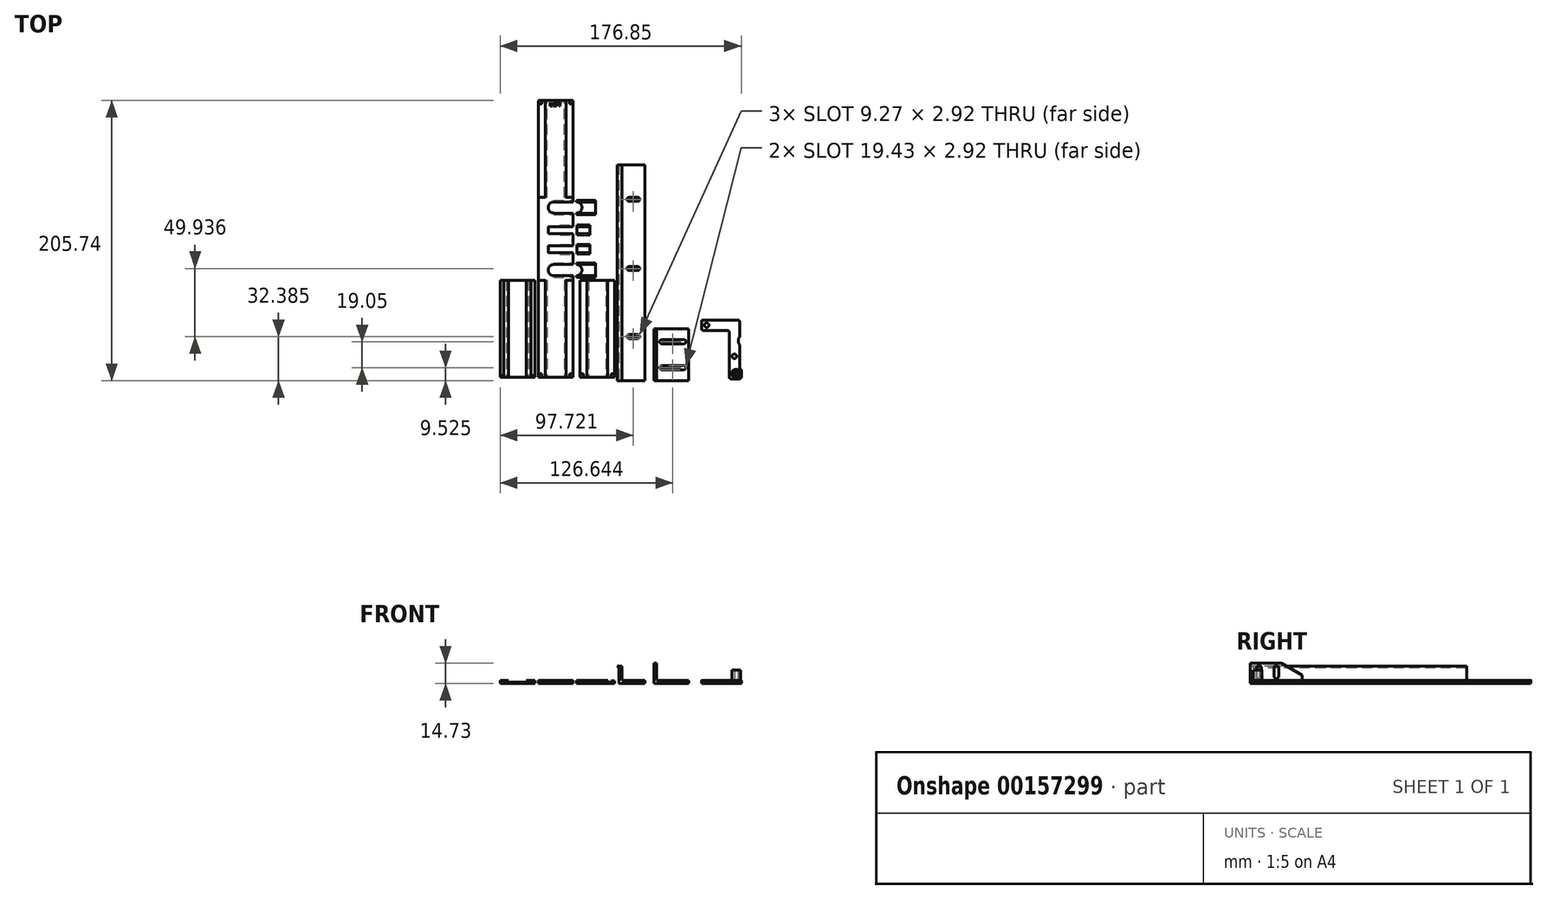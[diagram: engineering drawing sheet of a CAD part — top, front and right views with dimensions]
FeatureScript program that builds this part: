
annotation { "Feature Type Name" : "Feature", "Feature Type Description" : "" }
export const myFeature = defineFeature(function(context is Context, id is Id, definition is map)
    precondition{}
    {
        {
            var Q0;
            Q0=qCreatedBy(makeId("Top.planeOp"),FACE);
            var sketch = newSketch(context, id + "F0", { "sketchPlane" : qUnion([Q0])});
            skLineSegment(sketch, "E0.bottom", {"start": v(-2.54, 205.74) * mm, "end": v(-27.94, 205.74) * mm});
            skLineSegment(sketch, "E0.top", {"start": v(-2.54, 2.54) * mm, "end": v(-27.94, 2.54) * mm});
            skLineSegment(sketch, "E0.left", {"start": v(-2.54, 205.74) * mm, "end": v(-2.54, 131.27) * mm});
            skLineSegment(sketch, "E0.right", {"start": v(-27.94, 205.74) * mm, "end": v(-27.94, 2.54) * mm});
            skLineSegment(sketch, "E1.bottom", {"start": v(-30.48, 2.54) * mm, "end": v(-55.88, 2.54) * mm});
            skLineSegment(sketch, "E1.top", {"start": v(-30.48, 73.66) * mm, "end": v(-55.88, 73.66) * mm});
            skLineSegment(sketch, "E1.left", {"start": v(-30.48, 2.54) * mm, "end": v(-30.48, 73.66) * mm});
            skLineSegment(sketch, "E1.right", {"start": v(-55.88, 2.54) * mm, "end": v(-55.88, 73.66) * mm});
            skLineSegment(sketch, "E2.MirrorCS", {"start": v(2.54, 2.54) * mm, "end": v(2.54, 73.66) * mm});
            skLineSegment(sketch, "E3.MirrorCS", {"start": v(2.54, 73.66) * mm, "end": v(27.94, 73.66) * mm});
            skLineSegment(sketch, "E4.MirrorCS", {"start": v(27.94, 2.54) * mm, "end": v(27.94, 73.66) * mm});
            skLineSegment(sketch, "E5.MirrorCS", {"start": v(2.54, 2.54) * mm, "end": v(27.94, 2.54) * mm});
            skPoint(sketch, "E6.MirrorCS.start.orphan", {"position": v(-30.48, 73.66) * mm});
            skArc(sketch, "E7", {"start": v(-16.51, 131.27) * mm, "mid": v(-20.64, 127.14) * mm, "end": v(-16.51, 123.01) * mm});
            skArc(sketch, "E8", {"start": v(-16.51, 85.3) * mm, "mid": v(-20.64, 81.17) * mm, "end": v(-16.51, 77.04) * mm});
            skLineSegment(sketch, "E9", {"start": v(-16.51, 131.27) * mm, "end": v(-2.54, 131.27) * mm});
            skLineSegment(sketch, "E10", {"start": v(-16.51, 123.01) * mm, "end": v(-2.54, 123.01) * mm});
            skLineSegment(sketch, "E11", {"start": v(-16.51, 85.3) * mm, "end": v(-2.54, 85.3) * mm});
            skLineSegment(sketch, "E12", {"start": v(-16.51, 77.04) * mm, "end": v(-2.54, 77.04) * mm});
            skLineSegment(sketch, "E13.bottom", {"start": v(0, 77.04) * mm, "end": v(13.97, 77.04) * mm});
            skLineSegment(sketch, "E13.top", {"start": v(0, 85.3) * mm, "end": v(13.97, 85.3) * mm});
            skLineSegment(sketch, "E13.right", {"start": v(13.97, 77.04) * mm, "end": v(13.97, 85.3) * mm});
            skLineSegment(sketch, "E14.bottom", {"start": v(0, 123.01) * mm, "end": v(13.97, 123.01) * mm});
            skLineSegment(sketch, "E14.top", {"start": v(0, 131.27) * mm, "end": v(13.97, 131.27) * mm});
            skLineSegment(sketch, "E14.right", {"start": v(13.97, 123.01) * mm, "end": v(13.97, 131.27) * mm});
            skArc(sketch, "E15", {"start": v(0, 77.04) * mm, "mid": v(4.13, 81.17) * mm, "end": v(0, 85.3) * mm});
            skArc(sketch, "E16", {"start": v(0, 123.01) * mm, "mid": v(4.13, 127.14) * mm, "end": v(0, 131.27) * mm});
            skLineSegment(sketch, "E17.bottom", {"start": v(-2.54, 93.87) * mm, "end": v(-20.13, 93.87) * mm});
            skLineSegment(sketch, "E17.top", {"start": v(-2.54, 98.95) * mm, "end": v(-20.13, 98.95) * mm});
            skLineSegment(sketch, "E17.right", {"start": v(-20.64, 94.37) * mm, "end": v(-20.64, 98.44) * mm});
            skLineSegment(sketch, "E18.bottom", {"start": v(-2.54, 108.09) * mm, "end": v(-20.13, 108.09) * mm});
            skLineSegment(sketch, "E18.top", {"start": v(-2.54, 113.17) * mm, "end": v(-20.13, 113.17) * mm});
            skLineSegment(sketch, "E18.right", {"start": v(-20.64, 108.6) * mm, "end": v(-20.64, 112.66) * mm});
            skPoint(sketch, "E19.visualSharp", {"position": v(-20.64, 113.17) * mm});
            skArc(sketch, "E19.filletArc", {"start": v(-20.13, 113.17) * mm, "mid": v(-20.49, 113.02) * mm, "end": v(-20.64, 112.66) * mm});
            skPoint(sketch, "E20.visualSharp", {"position": v(-20.64, 108.09) * mm});
            skArc(sketch, "E20.filletArc", {"start": v(-20.64, 108.6) * mm, "mid": v(-20.49, 108.24) * mm, "end": v(-20.13, 108.09) * mm});
            skPoint(sketch, "E21.visualSharp", {"position": v(-20.64, 98.95) * mm});
            skArc(sketch, "E21.filletArc", {"start": v(-20.13, 98.95) * mm, "mid": v(-20.49, 98.8) * mm, "end": v(-20.64, 98.44) * mm});
            skPoint(sketch, "E22.visualSharp", {"position": v(-20.64, 93.87) * mm});
            skArc(sketch, "E22.filletArc", {"start": v(-20.64, 94.37) * mm, "mid": v(-20.49, 94.01) * mm, "end": v(-20.13, 93.87) * mm});
            skLineSegment(sketch, "E23.bottom", {"start": v(0.42, 113.17) * mm, "end": v(9.95, 113.17) * mm});
            skLineSegment(sketch, "E23.top", {"start": v(0.42, 108.09) * mm, "end": v(9.95, 108.09) * mm});
            skLineSegment(sketch, "E23.left", {"start": v(0.42, 113.17) * mm, "end": v(0.42, 108.09) * mm});
            skLineSegment(sketch, "E23.right", {"start": v(9.95, 113.17) * mm, "end": v(9.95, 108.09) * mm});
            skLineSegment(sketch, "E24.bottom", {"start": v(0.42, 98.95) * mm, "end": v(9.95, 98.95) * mm});
            skLineSegment(sketch, "E24.top", {"start": v(0.42, 93.9) * mm, "end": v(9.95, 93.9) * mm});
            skLineSegment(sketch, "E24.left", {"start": v(0.42, 98.95) * mm, "end": v(0.42, 93.9) * mm});
            skLineSegment(sketch, "E24.right", {"start": v(9.95, 98.95) * mm, "end": v(9.95, 93.9) * mm});
            skLineSegment(sketch, "E25.trimOffspring", {"start": v(-2.54, 77.04) * mm, "end": v(-2.54, 2.54) * mm});
            skLineSegment(sketch, "E26.trimOffspring", {"start": v(-2.54, 123.01) * mm, "end": v(-2.54, 113.17) * mm});
            skLineSegment(sketch, "E27.trimOffspring", {"start": v(-2.54, 108.09) * mm, "end": v(-2.54, 98.95) * mm});
            skLineSegment(sketch, "E28.trimOffspring", {"start": v(-2.54, 93.87) * mm, "end": v(-2.54, 85.3) * mm});
            skSolve(sketch);
        }
        {
            var Q0;
            Q0 = qSketchRegion(id + "F0", true);
            extrude(context, id + "F1", {"entities" : qUnion([Q0]), "depth" : 2.3 * mm});
        }
        {
            var Q0;
            Q0=makeQuery(id+"F1.opExtrude","SWEPT_FACE",FACE,{"disambiguationData":[OSD([sQuery(id+"F0.wireOp",EDGE,"E0.top")])]});
            var sketch = newSketch(context, id + "F2", { "sketchPlane" : qUnion([Q0])});
            skLineSegment(sketch, "E29", {"start": v(-22.81, 1.98) * mm, "end": v(-21.59, 0.76) * mm});
            skLineSegment(sketch, "E30", {"start": v(-21.59, 0.76) * mm, "end": v(-27.94, 0.76) * mm});
            skLineSegment(sketch, "E31", {"start": v(-27.94, 0.76) * mm, "end": v(-27.94, 2.29) * mm});
            skLineSegment(sketch, "E32", {"start": v(-8.9, 0.76) * mm, "end": v(-7.67, 1.98) * mm});
            skLineSegment(sketch, "E33", {"start": v(-2.54, 2.29) * mm, "end": v(-2.54, 0.76) * mm});
            skLineSegment(sketch, "E34", {"start": v(-2.54, 0.76) * mm, "end": v(-8.9, 0.76) * mm});
            skPoint(sketch, "E35.visualSharp", {"position": v(-23.11, 2.29) * mm});
            skArc(sketch, "E36.filletArc", {"start": v(-22.68, 2.29) * mm, "mid": v(-22.85, 2.18) * mm, "end": v(-22.81, 1.98) * mm});
            skArc(sketch, "E37.filletArc", {"start": v(-7.67, 1.98) * mm, "mid": v(-7.63, 2.18) * mm, "end": v(-7.8, 2.29) * mm});
            skLineSegment(sketch, "E38", {"start": v(-7.8, 2.29) * mm, "end": v(-2.54, 2.29) * mm});
            skLineSegment(sketch, "E39", {"start": v(-27.94, 2.29) * mm, "end": v(-22.68, 2.29) * mm});
            skLineSegment(sketch, "E40", {"start": v(-49.78, 2.29) * mm, "end": v(-51.3, 0.76) * mm});
            skLineSegment(sketch, "E41", {"start": v(-35.05, 0.76) * mm, "end": v(-36.58, 2.29) * mm});
            skLineSegment(sketch, "E42", {"start": v(-36.58, 2.29) * mm, "end": v(-49.78, 2.29) * mm});
            skLineSegment(sketch, "E43", {"start": v(-51.3, 0.76) * mm, "end": v(-35.05, 0.76) * mm});
            skLineSegment(sketch, "E44.MirrorCS", {"start": v(2.54, 2.29) * mm, "end": v(2.54, 0.76) * mm});
            skLineSegment(sketch, "E45.MirrorCS", {"start": v(2.54, 0.76) * mm, "end": v(8.9, 0.76) * mm});
            skLineSegment(sketch, "E46.MirrorCS", {"start": v(8.9, 0.76) * mm, "end": v(7.67, 1.98) * mm});
            skLineSegment(sketch, "E47.MirrorCS", {"start": v(7.8, 2.29) * mm, "end": v(2.54, 2.29) * mm});
            skArc(sketch, "E48.MirrorCS", {"start": v(7.67, 1.98) * mm, "mid": v(7.63, 2.18) * mm, "end": v(7.8, 2.29) * mm});
            skLineSegment(sketch, "E49.MirrorCS", {"start": v(27.94, 0.76) * mm, "end": v(27.94, 2.29) * mm});
            skLineSegment(sketch, "E50.MirrorCS", {"start": v(27.94, 2.29) * mm, "end": v(22.68, 2.29) * mm});
            skLineSegment(sketch, "E51.MirrorCS", {"start": v(21.59, 0.76) * mm, "end": v(27.94, 0.76) * mm});
            skLineSegment(sketch, "E52.MirrorCS", {"start": v(22.81, 1.98) * mm, "end": v(21.59, 0.76) * mm});
            skArc(sketch, "E53.MirrorCS", {"start": v(22.68, 2.29) * mm, "mid": v(22.85, 2.18) * mm, "end": v(22.81, 1.98) * mm});
            skSolve(sketch);
        }
        {
            var Q0;
            Q0 = qSketchRegion(id + "F2", true);
            extrude(context, id + "F3", {"entities" : qUnion([Q0]), "operationType" : NewBodyOperationType.REMOVE, "oppositeDirection" : true, "depth" : 71.12 * mm});
        }
        {
            var Q0;
            Q0=makeQuery(id+"F1.opExtrude","SWEPT_FACE",FACE,{"disambiguationData":[OSD([sQuery(id+"F0.wireOp",EDGE,"E0.bottom")])]});
            var sketch = newSketch(context, id + "F4", { "sketchPlane" : qUnion([Q0])});
            skLineSegment(sketch, "E54", {"start": v(7.67, 1.98) * mm, "end": v(8.9, 0.76) * mm});
            skLineSegment(sketch, "E55", {"start": v(8.9, 0.76) * mm, "end": v(2.54, 0.76) * mm});
            skLineSegment(sketch, "E56", {"start": v(2.54, 0.76) * mm, "end": v(2.54, 2.29) * mm});
            skLineSegment(sketch, "E57", {"start": v(21.59, 0.76) * mm, "end": v(22.81, 1.98) * mm});
            skLineSegment(sketch, "E58", {"start": v(27.94, 2.29) * mm, "end": v(27.94, 0.76) * mm});
            skLineSegment(sketch, "E59", {"start": v(27.94, 0.76) * mm, "end": v(21.59, 0.76) * mm});
            skPoint(sketch, "E60.visualSharp", {"position": v(7.37, 2.28) * mm});
            skArc(sketch, "E61.filletArc", {"start": v(7.8, 2.29) * mm, "mid": v(7.63, 2.18) * mm, "end": v(7.67, 1.98) * mm});
            skArc(sketch, "E62.filletArc", {"start": v(22.81, 1.98) * mm, "mid": v(22.85, 2.18) * mm, "end": v(22.68, 2.29) * mm});
            skLineSegment(sketch, "E63", {"start": v(22.68, 2.29) * mm, "end": v(27.94, 2.29) * mm});
            skLineSegment(sketch, "E64", {"start": v(2.54, 2.29) * mm, "end": v(7.8, 2.29) * mm});
            skSolve(sketch);
        }
        {
            var Q0;
            Q0 = qSketchRegion(id + "F4", true);
            extrude(context, id + "F5", {"entities" : qUnion([Q0]), "operationType" : NewBodyOperationType.REMOVE, "oppositeDirection" : true, "depth" : 71.12 * mm});
        }
        {
            var Q0;
            Q0=makeQuery(id+"F3.boolean.opBoolean","COPY",FACE,{"derivedFrom":makeQuery(id+"F3.opExtrude","SWEPT_FACE",FACE,{"disambiguationData":[OSD([sQuery(id+"F2.wireOp",EDGE,"E34")])]})});
            var sketch = newSketch(context, id + "F6", { "sketchPlane" : qUnion([Q0])});
            skLineSegment(sketch, "E65.bottom", {"start": v(-2.54, 2.54) * mm, "end": v(-5.08, 2.54) * mm});
            skLineSegment(sketch, "E65.top", {"start": v(-2.54, 5.08) * mm, "end": v(-5.08, 5.08) * mm});
            skLineSegment(sketch, "E65.left", {"start": v(-2.54, 2.54) * mm, "end": v(-2.54, 5.08) * mm});
            skLineSegment(sketch, "E65.right", {"start": v(-5.08, 2.54) * mm, "end": v(-5.08, 5.08) * mm});
            skLineSegment(sketch, "E66.bottom", {"start": v(-25.4, 2.54) * mm, "end": v(-27.94, 2.54) * mm});
            skLineSegment(sketch, "E66.top", {"start": v(-25.4, 5.08) * mm, "end": v(-27.94, 5.08) * mm});
            skLineSegment(sketch, "E66.left", {"start": v(-25.4, 2.54) * mm, "end": v(-25.4, 5.08) * mm});
            skLineSegment(sketch, "E66.right", {"start": v(-27.94, 2.54) * mm, "end": v(-27.94, 5.08) * mm});
            skLineSegment(sketch, "E67.bottom", {"start": v(27.94, 2.54) * mm, "end": v(25.4, 2.54) * mm});
            skLineSegment(sketch, "E67.top", {"start": v(27.94, 5.08) * mm, "end": v(25.4, 5.08) * mm});
            skLineSegment(sketch, "E67.left", {"start": v(27.94, 2.54) * mm, "end": v(27.94, 5.08) * mm});
            skLineSegment(sketch, "E67.right", {"start": v(25.4, 2.54) * mm, "end": v(25.4, 5.08) * mm});
            skLineSegment(sketch, "E68.bottom", {"start": v(5.08, 2.54) * mm, "end": v(2.54, 2.54) * mm});
            skLineSegment(sketch, "E68.top", {"start": v(5.08, 5.08) * mm, "end": v(2.54, 5.08) * mm});
            skLineSegment(sketch, "E68.left", {"start": v(5.08, 2.54) * mm, "end": v(5.08, 5.08) * mm});
            skLineSegment(sketch, "E68.right", {"start": v(2.54, 2.54) * mm, "end": v(2.54, 5.08) * mm});
            skLineSegment(sketch, "E69.bottom", {"start": v(-27.94, 205.74) * mm, "end": v(-25.4, 205.74) * mm});
            skLineSegment(sketch, "E69.top", {"start": v(-27.94, 203.2) * mm, "end": v(-25.4, 203.2) * mm});
            skLineSegment(sketch, "E69.left", {"start": v(-27.94, 205.74) * mm, "end": v(-27.94, 203.2) * mm});
            skLineSegment(sketch, "E69.right", {"start": v(-25.4, 205.74) * mm, "end": v(-25.4, 203.2) * mm});
            skLineSegment(sketch, "E70.bottom", {"start": v(-5.08, 205.74) * mm, "end": v(-2.54, 205.74) * mm});
            skLineSegment(sketch, "E70.top", {"start": v(-5.08, 203.2) * mm, "end": v(-2.54, 203.2) * mm});
            skLineSegment(sketch, "E70.left", {"start": v(-5.08, 205.74) * mm, "end": v(-5.08, 203.2) * mm});
            skLineSegment(sketch, "E70.right", {"start": v(-2.54, 205.74) * mm, "end": v(-2.54, 203.2) * mm});
            skSolve(sketch);
        }
        {
            var Q0;
            Q0 = qSketchRegion(id + "F6", true);
            extrude(context, id + "F7", {"entities" : qUnion([Q0]), "operationType" : NewBodyOperationType.ADD, "depth" : 1.14 * mm});
        }
        {
            var Q0;
            {var subQ0=sQuery(id+"F0.wireOp",EDGE,"E1.bottom");var subQ1=sQuery(id+"F0.wireOp",EDGE,"E1.top");var subQ2=sQuery(id+"F0.wireOp",EDGE,"E1.right");Q0=makeQuery(id+"F3.boolean.opBoolean","SPLIT",FACE,{"disambiguationData":[TD([makeQuery(id+"F1.opExtrude","SWEPT_FACE",FACE,{"disambiguationData":[OSD([subQ2])]})])],"derivedFrom":makeQuery(id+"F1.opExtrude","CAP_FACE",FACE,{"disambiguationData":[OSD([subQ0,subQ1,sQuery(id+"F0.wireOp",EDGE,"E1.left"),subQ2])],"isStart":false})});}
            var sketch = newSketch(context, id + "F8", { "sketchPlane" : qUnion([Q0])});
            skLineSegment(sketch, "E71.bottom", {"start": v(-30.48, 3.8) * mm, "end": v(-33.27, 3.8) * mm});
            skLineSegment(sketch, "E71.top", {"start": v(-30.48, 73.66) * mm, "end": v(-33.27, 73.66) * mm});
            skLineSegment(sketch, "E71.left", {"start": v(-30.48, 3.8) * mm, "end": v(-30.48, 73.66) * mm});
            skLineSegment(sketch, "E71.right", {"start": v(-33.27, 3.8) * mm, "end": v(-33.27, 73.66) * mm});
            skLineSegment(sketch, "E72.bottom", {"start": v(-53.09, 3.8) * mm, "end": v(-55.88, 3.8) * mm});
            skLineSegment(sketch, "E72.top", {"start": v(-53.09, 73.66) * mm, "end": v(-55.88, 73.66) * mm});
            skLineSegment(sketch, "E72.left", {"start": v(-53.09, 3.8) * mm, "end": v(-53.09, 73.66) * mm});
            skLineSegment(sketch, "E72.right", {"start": v(-55.88, 3.8) * mm, "end": v(-55.88, 73.66) * mm});
            skSolve(sketch);
        }
        {
            var Q0;
            Q0 = qSketchRegion(id + "F8", true);
            extrude(context, id + "F9", {"entities" : qUnion([Q0]), "operationType" : NewBodyOperationType.REMOVE, "oppositeDirection" : true, "depth" : 1.27 * mm});
        }
        {
            var Q0;
            Q0=makeQuery(id+"F1.opExtrude","SWEPT_FACE",FACE,{"disambiguationData":[OSD([sQuery(id+"F0.wireOp",EDGE,"E28.trimOffspring")])]});
            var sketch = newSketch(context, id + "F10", { "sketchPlane" : qUnion([Q0])});
            skLineSegment(sketch, "E73", {"start": v(85.3, 2.29) * mm, "end": v(86.44, 1.14) * mm});
            skLineSegment(sketch, "E74", {"start": v(86.44, 1.14) * mm, "end": v(85.3, 0) * mm});
            skLineSegment(sketch, "E75", {"start": v(123.01, 2.29) * mm, "end": v(121.87, 1.14) * mm});
            skLineSegment(sketch, "E76", {"start": v(121.87, 1.14) * mm, "end": v(123.01, 0) * mm});
            skLineSegment(sketch, "E77", {"start": v(123.01, 0) * mm, "end": v(123.01, 2.29) * mm});
            skLineSegment(sketch, "E78", {"start": v(131.27, 2.29) * mm, "end": v(132.41, 1.14) * mm});
            skLineSegment(sketch, "E79", {"start": v(132.41, 1.14) * mm, "end": v(131.27, 0) * mm});
            skLineSegment(sketch, "E80", {"start": v(131.27, 0) * mm, "end": v(131.27, 2.29) * mm});
            skLineSegment(sketch, "E81", {"start": v(85.3, 2.29) * mm, "end": v(85.3, 0) * mm});
            skLineSegment(sketch, "E82", {"start": v(77.04, 2.29) * mm, "end": v(75.9, 1.14) * mm});
            skLineSegment(sketch, "E83", {"start": v(75.9, 1.14) * mm, "end": v(77.04, 0) * mm});
            skLineSegment(sketch, "E84", {"start": v(77.04, 0) * mm, "end": v(77.04, 2.29) * mm});
            skSolve(sketch);
        }
        {
            var Q0;
            Q0 = qSketchRegion(id + "F10", true);
            extrude(context, id + "F11", {"entities" : qUnion([Q0]), "operationType" : NewBodyOperationType.REMOVE, "oppositeDirection" : true, "depth" : 13.97 * mm});
        }
        {
            var Q0;
            Q0=makeQuery(id+"F1.opExtrude","SWEPT_FACE",FACE,{"disambiguationData":[OSD([sQuery(id+"F0.wireOp",EDGE,"E13.right")])]});
            var sketch = newSketch(context, id + "F12", { "sketchPlane" : qUnion([Q0])});
            skLineSegment(sketch, "E85", {"start": v(77.04, 2.16) * mm, "end": v(76.02, 1.14) * mm});
            skLineSegment(sketch, "E86", {"start": v(76.02, 1.14) * mm, "end": v(77.04, 0.13) * mm});
            skLineSegment(sketch, "E87", {"start": v(77.04, 0.13) * mm, "end": v(77.04, 2.16) * mm});
            skLineSegment(sketch, "E88", {"start": v(85.3, 0.13) * mm, "end": v(86.3, 1.14) * mm});
            skLineSegment(sketch, "E89", {"start": v(86.3, 1.14) * mm, "end": v(85.3, 2.16) * mm});
            skLineSegment(sketch, "E90", {"start": v(85.3, 2.16) * mm, "end": v(85.3, 0.13) * mm});
            skLineSegment(sketch, "E91", {"start": v(123.01, 2.16) * mm, "end": v(122, 1.14) * mm});
            skLineSegment(sketch, "E92", {"start": v(122, 1.14) * mm, "end": v(123.01, 0.13) * mm});
            skLineSegment(sketch, "E93", {"start": v(123.01, 0.13) * mm, "end": v(123.01, 2.16) * mm});
            skLineSegment(sketch, "E94", {"start": v(131.27, 0.13) * mm, "end": v(132.28, 1.14) * mm});
            skLineSegment(sketch, "E95", {"start": v(132.28, 1.14) * mm, "end": v(131.27, 2.16) * mm});
            skLineSegment(sketch, "E96", {"start": v(131.27, 2.16) * mm, "end": v(131.27, 0.13) * mm});
            skSolve(sketch);
        }
        {
            var Q0;
            Q0 = qSketchRegion(id + "F12", true);
            extrude(context, id + "F13", {"entities" : qUnion([Q0]), "operationType" : NewBodyOperationType.ADD, "oppositeDirection" : true, "depth" : 13.97 * mm});
        }
        {
            var Q0;
            Q0=makeQuery(id+"F1.opExtrude","SWEPT_FACE",FACE,{"disambiguationData":[OSD([sQuery(id+"F0.wireOp",EDGE,"E24.right")])]});
            var sketch = newSketch(context, id + "F14", { "sketchPlane" : qUnion([Q0])});
            skLineSegment(sketch, "E97", {"start": v(93.9, 2.16) * mm, "end": v(92.9, 1.14) * mm});
            skLineSegment(sketch, "E98", {"start": v(92.9, 1.14) * mm, "end": v(93.9, 0.13) * mm});
            skLineSegment(sketch, "E99", {"start": v(93.9, 0.13) * mm, "end": v(93.9, 2.16) * mm});
            skLineSegment(sketch, "E100", {"start": v(98.95, 2.16) * mm, "end": v(99.96, 1.14) * mm});
            skLineSegment(sketch, "E101", {"start": v(99.96, 1.14) * mm, "end": v(98.95, 0.13) * mm});
            skLineSegment(sketch, "E102", {"start": v(98.95, 0.13) * mm, "end": v(98.95, 2.16) * mm});
            skLineSegment(sketch, "E103", {"start": v(108.09, 2.16) * mm, "end": v(107.07, 1.14) * mm});
            skLineSegment(sketch, "E104", {"start": v(107.07, 1.14) * mm, "end": v(108.09, 0.13) * mm});
            skLineSegment(sketch, "E105", {"start": v(108.09, 0.13) * mm, "end": v(108.09, 2.16) * mm});
            skLineSegment(sketch, "E106", {"start": v(113.17, 2.16) * mm, "end": v(114.19, 1.14) * mm});
            skLineSegment(sketch, "E107", {"start": v(114.19, 1.14) * mm, "end": v(113.17, 0.13) * mm});
            skLineSegment(sketch, "E108", {"start": v(113.17, 0.13) * mm, "end": v(113.17, 2.16) * mm});
            skSolve(sketch);
        }
        {
            var Q0;
            Q0=makeQuery(id+"F1.opExtrude","SWEPT_FACE",FACE,{"disambiguationData":[OSD([sQuery(id+"F0.wireOp",EDGE,"E27.trimOffspring")])]});
            var sketch = newSketch(context, id + "F15", { "sketchPlane" : qUnion([Q0])});
            skLineSegment(sketch, "E109", {"start": v(93.87, 2.29) * mm, "end": v(92.72, 1.14) * mm});
            skLineSegment(sketch, "E110", {"start": v(92.72, 1.14) * mm, "end": v(93.87, 0) * mm});
            skLineSegment(sketch, "E111", {"start": v(93.87, 0) * mm, "end": v(93.87, 2.29) * mm});
            skLineSegment(sketch, "E112", {"start": v(98.95, 2.29) * mm, "end": v(100.09, 1.14) * mm});
            skLineSegment(sketch, "E113", {"start": v(100.09, 1.14) * mm, "end": v(98.95, 0) * mm});
            skLineSegment(sketch, "E114", {"start": v(98.95, 0) * mm, "end": v(98.95, 2.29) * mm});
            skLineSegment(sketch, "E115", {"start": v(113.17, 2.29) * mm, "end": v(114.31, 1.14) * mm});
            skLineSegment(sketch, "E116", {"start": v(114.31, 1.14) * mm, "end": v(113.17, 0) * mm});
            skLineSegment(sketch, "E117", {"start": v(113.17, 0) * mm, "end": v(113.17, 2.29) * mm});
            skLineSegment(sketch, "E118", {"start": v(108.09, 2.29) * mm, "end": v(106.95, 1.14) * mm});
            skLineSegment(sketch, "E119", {"start": v(106.95, 1.14) * mm, "end": v(108.09, 0) * mm});
            skLineSegment(sketch, "E120", {"start": v(108.09, 0) * mm, "end": v(108.09, 2.29) * mm});
            skSolve(sketch);
        }
        {
            var Q0;
            Q0 = qSketchRegion(id + "F15", true);
            extrude(context, id + "F16", {"entities" : qUnion([Q0]), "operationType" : NewBodyOperationType.REMOVE, "oppositeDirection" : true, "depth" : 9.52 * mm});
        }
        {
            var Q0;
            Q0 = qSketchRegion(id + "F14", true);
            extrude(context, id + "F17", {"entities" : qUnion([Q0]), "operationType" : NewBodyOperationType.ADD, "oppositeDirection" : true, "depth" : 9.52 * mm});
        }
        {
            var Q0;
            Q0=makeQuery(id+"F1.opExtrude","CAP_FACE",FACE,{"disambiguationData":[OSD([sQuery(id+"F0.wireOp",EDGE,"E0.bottom"),sQuery(id+"F0.wireOp",EDGE,"E0.top"),sQuery(id+"F0.wireOp",EDGE,"E0.left"),sQuery(id+"F0.wireOp",EDGE,"E0.right"),sQuery(id+"F0.wireOp",EDGE,"E7"),sQuery(id+"F0.wireOp",EDGE,"E8"),sQuery(id+"F0.wireOp",EDGE,"E9"),sQuery(id+"F0.wireOp",EDGE,"E10"),sQuery(id+"F0.wireOp",EDGE,"E11"),sQuery(id+"F0.wireOp",EDGE,"E12"),sQuery(id+"F0.wireOp",EDGE,"E17.bottom"),sQuery(id+"F0.wireOp",EDGE,"E17.top"),sQuery(id+"F0.wireOp",EDGE,"E17.right"),sQuery(id+"F0.wireOp",EDGE,"E18.bottom"),sQuery(id+"F0.wireOp",EDGE,"E18.top"),sQuery(id+"F0.wireOp",EDGE,"E18.right"),sQuery(id+"F0.wireOp",EDGE,"E19.filletArc"),sQuery(id+"F0.wireOp",EDGE,"E20.filletArc"),sQuery(id+"F0.wireOp",EDGE,"E21.filletArc"),sQuery(id+"F0.wireOp",EDGE,"E22.filletArc"),sQuery(id+"F0.wireOp",EDGE,"E25.trimOffspring"),sQuery(id+"F0.wireOp",EDGE,"E26.trimOffspring"),sQuery(id+"F0.wireOp",EDGE,"E27.trimOffspring"),sQuery(id+"F0.wireOp",EDGE,"E28.trimOffspring")])],"isStart":false});
            var sketch = newSketch(context, id + "F18", { "sketchPlane" : qUnion([Q0])});
            skText(sketch, "E121", { "text": "LEFT", "fontName": "OpenSans-Bold.ttf"});
            const initialGuessF18  = {"E121": [-0.01955, 0.20151, 1, 0, 0.0027]};
            skSetInitialGuess(sketch, initialGuessF18);
            skSolve(sketch);
        }
        {
            var Q0;
            Q0 = qSketchRegion(id + "F18", true);
            extrude(context, id + "F19", {"entities" : qUnion([Q0]), "operationType" : NewBodyOperationType.REMOVE, "oppositeDirection" : true, "depth" : 0.38 * mm});
        }
        {
            var Q0;
            Q0=qCreatedBy(makeId("Front.planeOp"),FACE);
            var sketch = newSketch(context, id + "F20", { "sketchPlane" : qUnion([Q0])});
            skLineSegment(sketch, "E122", {"start": v(31.3, 12.7) * mm, "end": v(31.3, 0) * mm});
            skLineSegment(sketch, "E123", {"start": v(31.3, 0) * mm, "end": v(50.35, 0) * mm});
            skLineSegment(sketch, "E124", {"start": v(50.35, 0) * mm, "end": v(50.35, 2.03) * mm});
            skLineSegment(sketch, "E125", {"start": v(50.35, 2.03) * mm, "end": v(33.33, 2.03) * mm});
            skLineSegment(sketch, "E126", {"start": v(33.33, 2.03) * mm, "end": v(33.33, 12.7) * mm});
            skLineSegment(sketch, "E127", {"start": v(31.3, 12.7) * mm, "end": v(33.33, 12.7) * mm});
            skSolve(sketch);
        }
        {
            var Q0;
            Q0 = qSketchRegion(id + "F20", true);
            extrude(context, id + "F21", {"entities" : qUnion([Q0]), "oppositeDirection" : true, "depth" : 158.52 * mm});
        }
        {
            var Q0;
            Q0=makeQuery(id+"F21.opExtrude","CAP_FACE",FACE,{"disambiguationData":[OSD([sQuery(id+"F20.wireOp",EDGE,"E122"),sQuery(id+"F20.wireOp",EDGE,"E123"),sQuery(id+"F20.wireOp",EDGE,"E124"),sQuery(id+"F20.wireOp",EDGE,"E125"),sQuery(id+"F20.wireOp",EDGE,"E126"),sQuery(id+"F20.wireOp",EDGE,"E127")])],"isStart":true});
            var sketch = newSketch(context, id + "F22", { "sketchPlane" : qUnion([Q0])});
            skLineSegment(sketch, "E128", {"start": v(31.3, 12.7) * mm, "end": v(30.03, 12.7) * mm});
            skLineSegment(sketch, "E129", {"start": v(30.03, 12.7) * mm, "end": v(31.3, 11.43) * mm});
            skLineSegment(sketch, "E130", {"start": v(31.3, 11.43) * mm, "end": v(31.3, 12.7) * mm});
            skSolve(sketch);
        }
        {
            var Q0;
            Q0 = qSketchRegion(id + "F22", true);
            extrude(context, id + "F23", {"entities" : qUnion([Q0]), "operationType" : NewBodyOperationType.ADD, "oppositeDirection" : true, "depth" : 158.52 * mm});
        }
        {
            var Q0;
            Q0=makeQuery(id+"F21.opExtrude","SWEPT_FACE",FACE,{"disambiguationData":[OSD([sQuery(id+"F20.wireOp",EDGE,"E125")])]});
            var sketch = newSketch(context, id + "F24", { "sketchPlane" : qUnion([Q0])});
            skArc(sketch, "E131", {"start": v(45.02, 30.92) * mm, "mid": v(46.48, 32.39) * mm, "end": v(45.02, 33.85) * mm});
            skArc(sketch, "E132", {"start": v(45.02, 131.66) * mm, "mid": v(46.48, 133.12) * mm, "end": v(45.02, 134.58) * mm});
            skArc(sketch, "E133", {"start": v(45.02, 80.86) * mm, "mid": v(46.48, 82.32) * mm, "end": v(45.02, 83.78) * mm});
            skArc(sketch, "E134", {"start": v(38.67, 134.58) * mm, "mid": v(37.2, 133.12) * mm, "end": v(38.67, 131.66) * mm});
            skArc(sketch, "E135", {"start": v(38.67, 83.78) * mm, "mid": v(37.2, 82.32) * mm, "end": v(38.67, 80.86) * mm});
            skArc(sketch, "E136", {"start": v(38.67, 33.85) * mm, "mid": v(37.2, 32.39) * mm, "end": v(38.67, 30.92) * mm});
            skLineSegment(sketch, "E137", {"start": v(45.02, 134.58) * mm, "end": v(38.67, 134.58) * mm});
            skLineSegment(sketch, "E138", {"start": v(38.67, 131.66) * mm, "end": v(45.02, 131.66) * mm});
            skLineSegment(sketch, "E139", {"start": v(38.67, 83.78) * mm, "end": v(45.02, 83.78) * mm});
            skLineSegment(sketch, "E140", {"start": v(38.67, 80.86) * mm, "end": v(45.02, 80.86) * mm});
            skLineSegment(sketch, "E141", {"start": v(38.67, 33.85) * mm, "end": v(45.02, 33.85) * mm});
            skLineSegment(sketch, "E142", {"start": v(45.02, 30.92) * mm, "end": v(38.67, 30.92) * mm});
            skSolve(sketch);
        }
        {
            var Q0;
            Q0 = qSketchRegion(id + "F24", true);
            extrude(context, id + "F25", {"entities" : qUnion([Q0]), "operationType" : NewBodyOperationType.REMOVE, "endBound" : BoundingType.UP_TO_NEXT, "oppositeDirection" : true, "depth" : 25.4 * mm});
        }
        {
            var Q0;
            Q0=qCreatedBy(makeId("Top.planeOp"),FACE);
            var sketch = newSketch(context, id + "F26", { "sketchPlane" : qUnion([Q0])});
            skLineSegment(sketch, "E143.bottom", {"start": v(56.92, 38.1) * mm, "end": v(82.32, 38.1) * mm});
            skLineSegment(sketch, "E143.top", {"start": v(56.92, 0) * mm, "end": v(82.32, 0) * mm});
            skLineSegment(sketch, "E143.left", {"start": v(56.92, 38.1) * mm, "end": v(56.92, 0) * mm});
            skLineSegment(sketch, "E143.right", {"start": v(82.32, 38.1) * mm, "end": v(82.32, 0) * mm});
            skArc(sketch, "E144", {"start": v(62.5, 30.04) * mm, "mid": v(61.05, 28.58) * mm, "end": v(62.5, 27.11) * mm});
            skArc(sketch, "E145", {"start": v(79.02, 27.11) * mm, "mid": v(80.48, 28.58) * mm, "end": v(79.02, 30.04) * mm});
            skArc(sketch, "E146", {"start": v(62.5, 10.99) * mm, "mid": v(61.05, 9.53) * mm, "end": v(62.5, 8.06) * mm});
            skArc(sketch, "E147", {"start": v(79.02, 8.06) * mm, "mid": v(80.48, 9.53) * mm, "end": v(79.02, 10.99) * mm});
            skLineSegment(sketch, "E148", {"start": v(62.5, 30.04) * mm, "end": v(79.02, 30.04) * mm});
            skLineSegment(sketch, "E149", {"start": v(79.02, 10.99) * mm, "end": v(62.5, 10.99) * mm});
            skLineSegment(sketch, "E150", {"start": v(62.5, 8.06) * mm, "end": v(79.02, 8.06) * mm});
            skLineSegment(sketch, "E151", {"start": v(62.5, 27.11) * mm, "end": v(79.02, 27.11) * mm});
            skSolve(sketch);
        }
        {
            var Q0;
            Q0 = qSketchRegion(id + "F26", true);
            extrude(context, id + "F27", {"entities" : qUnion([Q0]), "depth" : 2.03 * mm});
        }
        {
            var Q0;
            Q0=makeQuery(id+"F27.opExtrude","CAP_FACE",FACE,{"disambiguationData":[OSD([sQuery(id+"F26.wireOp",EDGE,"E143.bottom"),sQuery(id+"F26.wireOp",EDGE,"E143.top"),sQuery(id+"F26.wireOp",EDGE,"E143.left"),sQuery(id+"F26.wireOp",EDGE,"E143.right"),sQuery(id+"F26.wireOp",EDGE,"E144"),sQuery(id+"F26.wireOp",EDGE,"E145"),sQuery(id+"F26.wireOp",EDGE,"E146"),sQuery(id+"F26.wireOp",EDGE,"E147"),sQuery(id+"F26.wireOp",EDGE,"E148"),sQuery(id+"F26.wireOp",EDGE,"E149"),sQuery(id+"F26.wireOp",EDGE,"E150"),sQuery(id+"F26.wireOp",EDGE,"E151")])],"isStart":false});
            var sketch = newSketch(context, id + "F28", { "sketchPlane" : qUnion([Q0])});
            skLineSegment(sketch, "E152.bottom", {"start": v(56.92, 38.1) * mm, "end": v(58.95, 38.1) * mm});
            skLineSegment(sketch, "E152.top", {"start": v(56.92, 0) * mm, "end": v(58.95, 0) * mm});
            skLineSegment(sketch, "E152.left", {"start": v(56.92, 38.1) * mm, "end": v(56.92, 0) * mm});
            skLineSegment(sketch, "E152.right", {"start": v(58.95, 38.1) * mm, "end": v(58.95, 0) * mm});
            skSolve(sketch);
        }
        {
            var Q0;
            Q0 = qSketchRegion(id + "F28", true);
            extrude(context, id + "F29", {"entities" : qUnion([Q0]), "operationType" : NewBodyOperationType.ADD, "depth" : 12.7 * mm});
        }
        {
            var Q0;
            Q0=makeQuery(id+"F29.opExtrude","SWEPT_FACE",FACE,{"disambiguationData":[OSD([sQuery(id+"F28.wireOp",EDGE,"E152.right")])]});
            var sketch = newSketch(context, id + "F30", { "sketchPlane" : qUnion([Q0])});
            skArc(sketch, "E153", {"start": v(8, 11.56) * mm, "mid": v(6.35, 13.2) * mm, "end": v(4.7, 11.56) * mm});
            skArc(sketch, "E154", {"start": v(20.7, 11.56) * mm, "mid": v(19.05, 13.2) * mm, "end": v(17.4, 11.56) * mm});
            skArc(sketch, "E155", {"start": v(4.7, 5.2) * mm, "mid": v(6.35, 3.56) * mm, "end": v(8, 5.2) * mm});
            skArc(sketch, "E156", {"start": v(17.4, 5.2) * mm, "mid": v(19.05, 3.56) * mm, "end": v(20.7, 5.2) * mm});
            skLineSegment(sketch, "E157", {"start": v(4.7, 11.56) * mm, "end": v(4.7, 5.2) * mm});
            skLineSegment(sketch, "E158", {"start": v(8, 5.2) * mm, "end": v(8, 11.56) * mm});
            skLineSegment(sketch, "E159", {"start": v(17.4, 5.2) * mm, "end": v(17.4, 11.56) * mm});
            skLineSegment(sketch, "E160", {"start": v(20.7, 11.56) * mm, "end": v(20.7, 5.2) * mm});
            skLineSegment(sketch, "E161", {"start": v(22.86, 14.73) * mm, "end": v(38.1, 5.84) * mm});
            skLineSegment(sketch, "E162", {"start": v(38.1, 5.84) * mm, "end": v(38.1, 14.73) * mm});
            skLineSegment(sketch, "E163", {"start": v(38.1, 14.73) * mm, "end": v(22.86, 14.73) * mm});
            skSolve(sketch);
        }
        {
            var Q0;
            Q0 = qSketchRegion(id + "F30", true);
            extrude(context, id + "F31", {"entities" : qUnion([Q0]), "operationType" : NewBodyOperationType.REMOVE, "endBound" : BoundingType.UP_TO_NEXT, "oppositeDirection" : true, "depth" : 25.4 * mm});
        }
        {
            var Q0;
            Q0=qCreatedBy(makeId("Top.planeOp"),FACE);
            var sketch = newSketch(context, id + "F32", { "sketchPlane" : qUnion([Q0])});
            skLineSegment(sketch, "E164", {"start": v(112.08, 2.64) * mm, "end": v(112.08, 35.66) * mm});
            skLineSegment(sketch, "E165", {"start": v(91.76, 38.2) * mm, "end": v(91.76, 43.28) * mm});
            skLineSegment(sketch, "E166", {"start": v(93.03, 44.55) * mm, "end": v(118.43, 44.55) * mm});
            skLineSegment(sketch, "E167", {"start": v(119.7, 43.28) * mm, "end": v(119.7, 32.17) * mm});
            skLineSegment(sketch, "E168", {"start": v(119.7, 1.37) * mm, "end": v(113.35, 1.37) * mm});
            skCircle(sketch, "E169", {"center": v(95.57, 40.74) * mm, "radius": 1.65 * mm});
            skCircle(sketch, "E170", {"center": v(115.89, 17.88) * mm, "radius": 1.65 * mm});
            skLineSegment(sketch, "E171", {"start": v(93.03, 36.93) * mm, "end": v(110.8, 36.93) * mm});
            skPoint(sketch, "E172.visualSharp", {"position": v(119.7, 44.55) * mm});
            skArc(sketch, "E172.filletArc", {"start": v(119.7, 43.28) * mm, "mid": v(119.33, 44.18) * mm, "end": v(118.43, 44.55) * mm});
            skPoint(sketch, "E173.visualSharp", {"position": v(112.08, 36.93) * mm});
            skArc(sketch, "E173.filletArc", {"start": v(112.08, 35.66) * mm, "mid": v(111.7, 36.56) * mm, "end": v(110.8, 36.93) * mm});
            skPoint(sketch, "E174.visualSharp", {"position": v(91.76, 44.55) * mm});
            skArc(sketch, "E174.filletArc", {"start": v(93.03, 44.55) * mm, "mid": v(92.13, 44.18) * mm, "end": v(91.76, 43.28) * mm});
            skPoint(sketch, "E175.visualSharp", {"position": v(91.76, 36.93) * mm});
            skArc(sketch, "E175.filletArc", {"start": v(91.76, 38.2) * mm, "mid": v(92.13, 37.3) * mm, "end": v(93.03, 36.93) * mm});
            skLineSegment(sketch, "E176", {"start": v(120.32, 8.62) * mm, "end": v(120.35, 8.6) * mm});
            skLineSegment(sketch, "E177", {"start": v(120.97, 7.51) * mm, "end": v(120.97, 2.64) * mm});
            skLineSegment(sketch, "E178", {"start": v(119.7, 1.37) * mm, "end": v(119.7, 1.37) * mm});
            skArc(sketch, "E179", {"start": v(119.7, 32.17) * mm, "mid": v(118.75, 29.31) * mm, "end": v(119.7, 26.46) * mm});
            skLineSegment(sketch, "E180.trimOffspring", {"start": v(119.7, 26.46) * mm, "end": v(119.7, 9.71) * mm});
            skPoint(sketch, "E181.visualSharp", {"position": v(120.97, 8.24) * mm});
            skArc(sketch, "E181.filletArc", {"start": v(120.97, 7.51) * mm, "mid": v(120.8, 8.14) * mm, "end": v(120.35, 8.6) * mm});
            skPoint(sketch, "E182.visualSharp", {"position": v(120.97, 1.37) * mm});
            skArc(sketch, "E182.filletArc", {"start": v(119.7, 1.37) * mm, "mid": v(120.6, 1.74) * mm, "end": v(120.97, 2.64) * mm});
            skPoint(sketch, "E183.visualSharp", {"position": v(112.08, 1.37) * mm});
            skArc(sketch, "E183.filletArc", {"start": v(112.08, 2.64) * mm, "mid": v(112.45, 1.74) * mm, "end": v(113.35, 1.37) * mm});
            skCircle(sketch, "E184", {"center": v(117.16, 5.18) * mm, "radius": 1.3 * mm});
            skPoint(sketch, "E185.visualSharp", {"position": v(119.7, 9) * mm});
            skArc(sketch, "E185.filletArc", {"start": v(119.7, 9.71) * mm, "mid": v(119.86, 9.09) * mm, "end": v(120.32, 8.62) * mm});
            skSolve(sketch);
        }
        {
            var Q0;
            Q0 = qSketchRegion(id + "F32", true);
            extrude(context, id + "F33", {"entities" : qUnion([Q0]), "depth" : 2.03 * mm});
        }
        {
            var Q0;
            Q0=makeQuery(id+"F33.opExtrude","CAP_FACE",FACE,{"disambiguationData":[OSD([sQuery(id+"F32.wireOp",EDGE,"E164"),sQuery(id+"F32.wireOp",EDGE,"E165"),sQuery(id+"F32.wireOp",EDGE,"E166"),sQuery(id+"F32.wireOp",EDGE,"E167"),sQuery(id+"F32.wireOp",EDGE,"E168"),sQuery(id+"F32.wireOp",EDGE,"E169"),sQuery(id+"F32.wireOp",EDGE,"E170"),sQuery(id+"F32.wireOp",EDGE,"E171"),sQuery(id+"F32.wireOp",EDGE,"E172.filletArc"),sQuery(id+"F32.wireOp",EDGE,"E173.filletArc"),sQuery(id+"F32.wireOp",EDGE,"E174.filletArc"),sQuery(id+"F32.wireOp",EDGE,"E175.filletArc"),sQuery(id+"F32.wireOp",EDGE,"E176"),sQuery(id+"F32.wireOp",EDGE,"E177"),sQuery(id+"F32.wireOp",EDGE,"E178"),sQuery(id+"F32.wireOp",EDGE,"E179"),sQuery(id+"F32.wireOp",EDGE,"E180.trimOffspring"),sQuery(id+"F32.wireOp",EDGE,"E181.filletArc"),sQuery(id+"F32.wireOp",EDGE,"E182.filletArc"),sQuery(id+"F32.wireOp",EDGE,"E183.filletArc"),sQuery(id+"F32.wireOp",EDGE,"E184")])],"isStart":false});
            var sketch = newSketch(context, id + "F34", { "sketchPlane" : qUnion([Q0])});
            skCircle(sketch, "E186", {"center": v(117.16, 5.18) * mm, "radius": 1.3 * mm});
            skCircle(sketch, "E187", {"center": v(117.16, 5.18) * mm, "radius": 3.18 * mm});
            skSolve(sketch);
        }
        {
            var Q0;
            Q0 = qSketchRegion(id + "F34", true);
            extrude(context, id + "F35", {"entities" : qUnion([Q0]), "operationType" : NewBodyOperationType.ADD, "depth" : 7.62 * mm});
        }
    });
